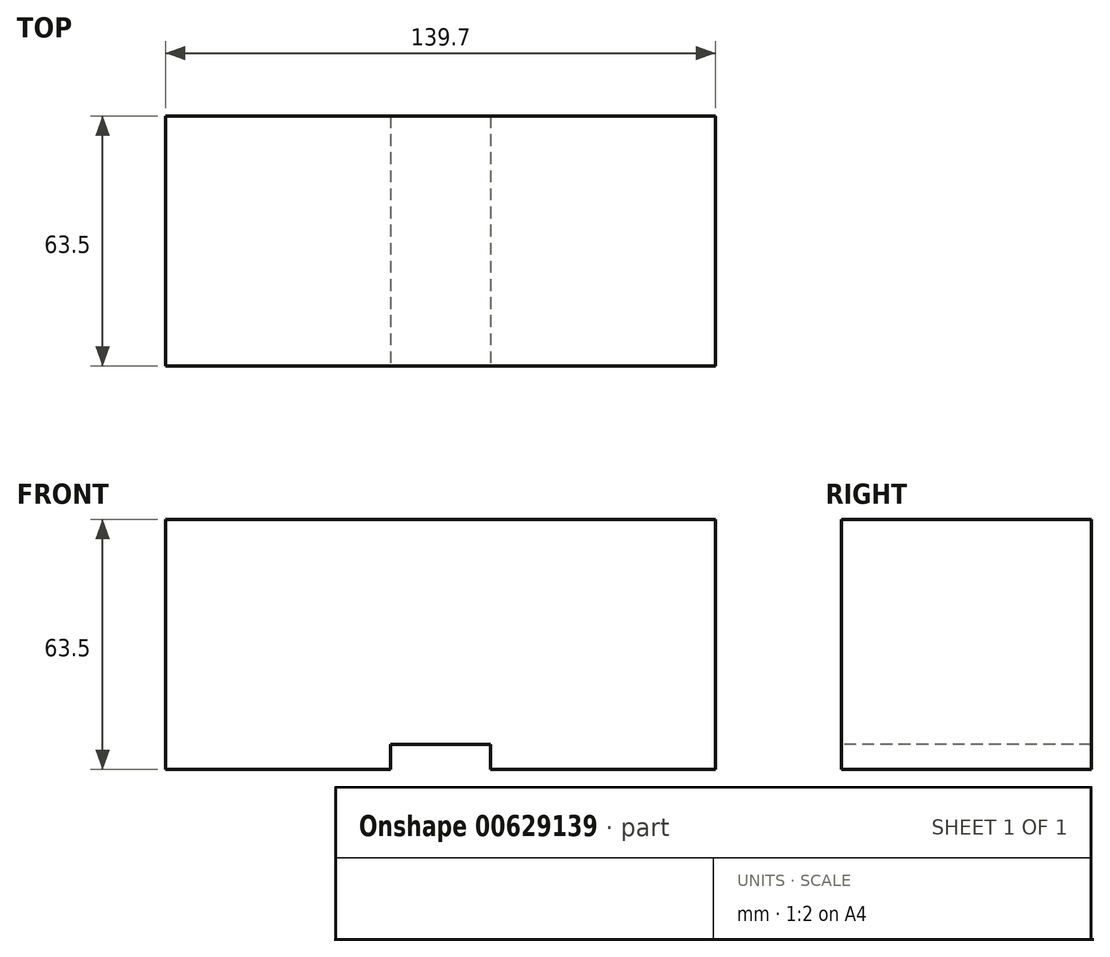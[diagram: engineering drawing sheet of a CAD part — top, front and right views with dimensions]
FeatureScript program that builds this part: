
annotation { "Feature Type Name" : "Feature", "Feature Type Description" : "" }
export const myFeature = defineFeature(function(context is Context, id is Id, definition is map)
    precondition{}
    {
        {
            var Q0;
            Q0=qCreatedBy(makeId("Front.planeOp"),FACE);
            var sketch = newSketch(context, id + "F0", { "sketchPlane" : qUnion([Q0])});
            skLineSegment(sketch, "E0.bottom", {"start": v(0, 0) * mm, "end": v(139.7, 0) * mm});
            skLineSegment(sketch, "E0.top", {"start": v(0, 63.5) * mm, "end": v(139.7, 63.5) * mm});
            skLineSegment(sketch, "E0.left", {"start": v(0, 0) * mm, "end": v(0, 63.5) * mm});
            skLineSegment(sketch, "E0.right", {"start": v(139.7, 0) * mm, "end": v(139.7, 63.5) * mm});
            skSolve(sketch);
        }
        {
            var Q0;
            Q0 = qSketchRegion(id + "F0", true);
            extrude(context, id + "F1", {"entities" : qUnion([Q0]), "depth" : 63.5 * mm, "offsetDistance" : 25.4 * mm});
        }
        {
            var Q0;
            Q0=makeQuery(id+"F1.opExtrude","CAP_FACE",FACE,{"disambiguationData":[OSD([sQuery(id+"F0.wireOp",EDGE,"E0.bottom"),sQuery(id+"F0.wireOp",EDGE,"E0.top"),sQuery(id+"F0.wireOp",EDGE,"E0.left"),sQuery(id+"F0.wireOp",EDGE,"E0.right")])],"isStart":false});
            var sketch = newSketch(context, id + "F2", { "sketchPlane" : qUnion([Q0])});
            skLineSegment(sketch, "E1.bottom", {"start": v(57.15, 0) * mm, "end": v(82.55, 0) * mm});
            skLineSegment(sketch, "E1.top", {"start": v(57.15, 6.35) * mm, "end": v(82.55, 6.35) * mm});
            skLineSegment(sketch, "E1.left", {"start": v(57.15, 0) * mm, "end": v(57.15, 6.35) * mm});
            skLineSegment(sketch, "E1.right", {"start": v(82.55, 0) * mm, "end": v(82.55, 6.35) * mm});
            skLineSegment(sketch, "E2", {"start": v(69.85, 63.5) * mm, "end": v(69.85, 6.35) * mm, "construction": true});
            skSolve(sketch);
        }
        {
            var Q0;
            Q0 = qSketchRegion(id + "F2", true);
            extrude(context, id + "F3", {"entities" : qUnion([Q0]), "operationType" : NewBodyOperationType.REMOVE, "endBound" : BoundingType.THROUGH_ALL, "oppositeDirection" : true, "depth" : 25.4 * mm, "offsetDistance" : 25.4 * mm});
        }
    });
